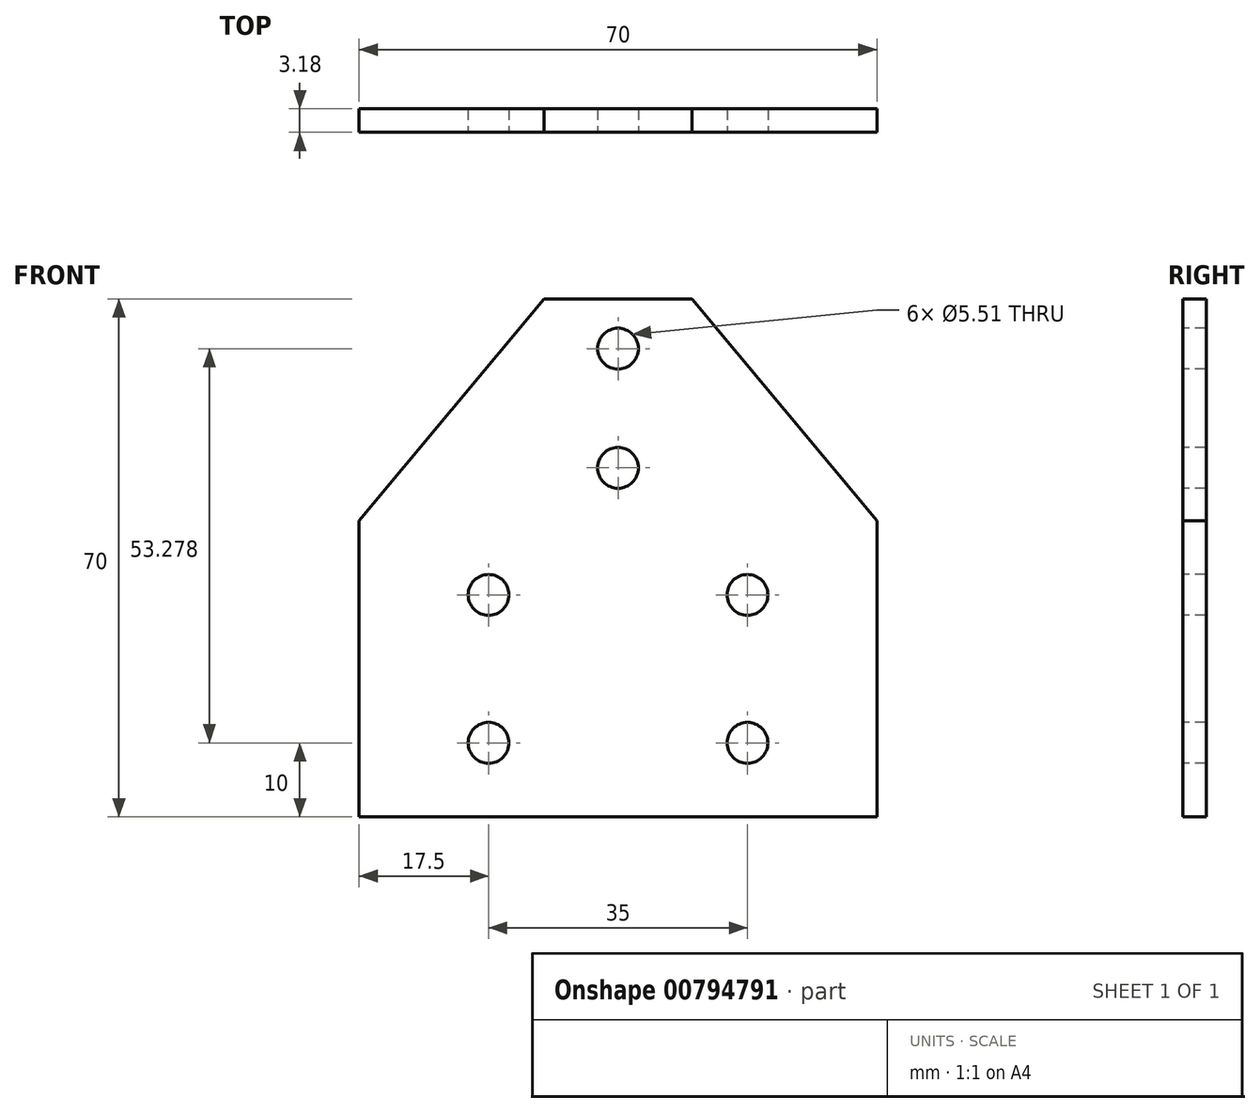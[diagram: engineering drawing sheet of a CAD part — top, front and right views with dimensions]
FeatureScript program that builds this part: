
annotation { "Feature Type Name" : "Feature", "Feature Type Description" : "" }
export const myFeature = defineFeature(function(context is Context, id is Id, definition is map)
    precondition{}
    {
        {
            var Q0;
            Q0=qCreatedBy(makeId("Front.planeOp"),FACE);
            var sketch = newSketch(context, id + "F0", { "sketchPlane" : qUnion([Q0])});
            skPoint(sketch, "E0", {"position": v(0, 0) * mm});
            skLineSegment(sketch, "E1.bottom", {"start": v(0, 0) * mm, "end": v(-70, 0) * mm});
            skLineSegment(sketch, "E1.left", {"start": v(0, 0) * mm, "end": v(0, 40) * mm});
            skLineSegment(sketch, "E1.right", {"start": v(-70, 0) * mm, "end": v(-70, 40) * mm});
            skPoint(sketch, "E2", {"position": v(-35, 0) * mm});
            skPoint(sketch, "E3", {"position": v(-25, 70) * mm});
            skLineSegment(sketch, "E4", {"start": v(-25, 70) * mm, "end": v(0, 40) * mm});
            skPoint(sketch, "E5", {"position": v(-45, 70) * mm});
            skLineSegment(sketch, "E6", {"start": v(-45, 70) * mm, "end": v(-70, 40) * mm});
            skLineSegment(sketch, "E7", {"start": v(-45, 70) * mm, "end": v(-25, 70) * mm});
            skPoint(sketch, "E8", {"position": v(-35, 63.28) * mm});
            skPoint(sketch, "E9", {"position": v(-35, 47.16) * mm});
            skPoint(sketch, "E10", {"position": v(-52.5, 0) * mm});
            skPoint(sketch, "E11", {"position": v(-17.5, 0) * mm});
            skPoint(sketch, "E12", {"position": v(-17.5, 10) * mm});
            skPoint(sketch, "E13", {"position": v(-17.5, 30) * mm});
            skPoint(sketch, "E14", {"position": v(-52.5, 10) * mm});
            skPoint(sketch, "E15", {"position": v(-52.5, 30) * mm});
            skPoint(sketch, "E16", {"position": v(-35, 20) * mm});
            skCircle(sketch, "E17", {"center": v(-35, 63.28) * mm, "radius": 2.76 * mm});
            skCircle(sketch, "E18", {"center": v(-35, 47.16) * mm, "radius": 2.76 * mm});
            skCircle(sketch, "E19", {"center": v(-17.5, 30) * mm, "radius": 2.76 * mm});
            skCircle(sketch, "E20", {"center": v(-52.5, 30) * mm, "radius": 2.76 * mm});
            skCircle(sketch, "E21", {"center": v(-52.5, 10) * mm, "radius": 2.76 * mm});
            skCircle(sketch, "E22", {"center": v(-17.5, 10) * mm, "radius": 2.76 * mm});
            skSolve(sketch);
        }
        {
            var Q0;
            Q0=makeQuery(id+"F0.imprint","IMPRINT",FACE,{"disambiguationData":[TD([[makeQuery(id+"F0.imprint","IMPRINT",EDGE,{"derivedFrom":sQuery(id+"F0.wireOp",EDGE,"E1.bottom")}),-1.0]])]});
            var Q1;
            {var subQ1=sQuery(id+"F0.wireOp",EDGE,"E4");Q1=makeQuery(id+"F0.imprint","IMPRINT",FACE,{"disambiguationData":[TD([[makeQuery(id+"F0.imprint","IMPRINT",EDGE,{"derivedFrom":subQ1}),-1.0]])]});}
            extrude(context, id + "F1", {"entities" : qUnion([Q0, Q1]), "oppositeDirection" : true, "depth" : 3.17 * mm, "offsetDistance" : 25.4 * mm});
        }
    });
